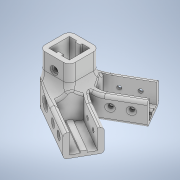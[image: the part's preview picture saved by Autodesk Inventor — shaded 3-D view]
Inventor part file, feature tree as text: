
AUTODESK INVENTOR PART (.ipt)
format: ipt  version: 2021 (Build 250183000, 183)  size: 554,496 bytes
history: native  units: mm
features: extrude x8, sketch x5, fillet x3, projected_geometry x3, mirror x2, other x1, chamfer x1
ambient origin geometry x8: Origin, YZ Plane, XZ Plane, XY Plane, X Axis, Y Axis, Z Axis, Center Point
bodies: Body1 (feature_tree)
feature tree (23):
  other  "솔리드1"
  sketch  "스케치1"
  extrude  "돌출1"  Depth=21.0mm
  extrude  "돌출4"  TaperAngle=60.0deg  [1 undecoded]
  sketch  "스케치2"
  extrude  "돌출5"  Depth=21.0mm
  extrude  "돌출6"  Depth=40.0mm
  mirror  "미러1"
  fillet  "모깎기1"  Radius=5.0mm
  fillet  "모깎기2"  Radius=5.0mm
  extrude  "돌출7"  Depth=5.0mm
  mirror  "미러2"
  chamfer  "모따기2"  Distance=20.0mm
  extrude  "돌출8"  Depth=5.0mm
  sketch  "스케치6"
  extrude  "돌출9"  Depth=50.0mm TaperAngle=0.0deg
  extrude  "돌출10"  Depth=4.3mm
  fillet  "모깎기4"  Radius=8.0mm
  projected_geometry  "투영된 루프1"
  sketch  "스케치3"
  projected_geometry  "투영된 루프2"
  sketch  "스케치4"
  projected_geometry  "투영된 루프5"
note: 1 required parameter value undecoded (feature->parameter linkage not recoverable at this tier; creation-order binding heuristic only, values carry confidence <= 0.55)
